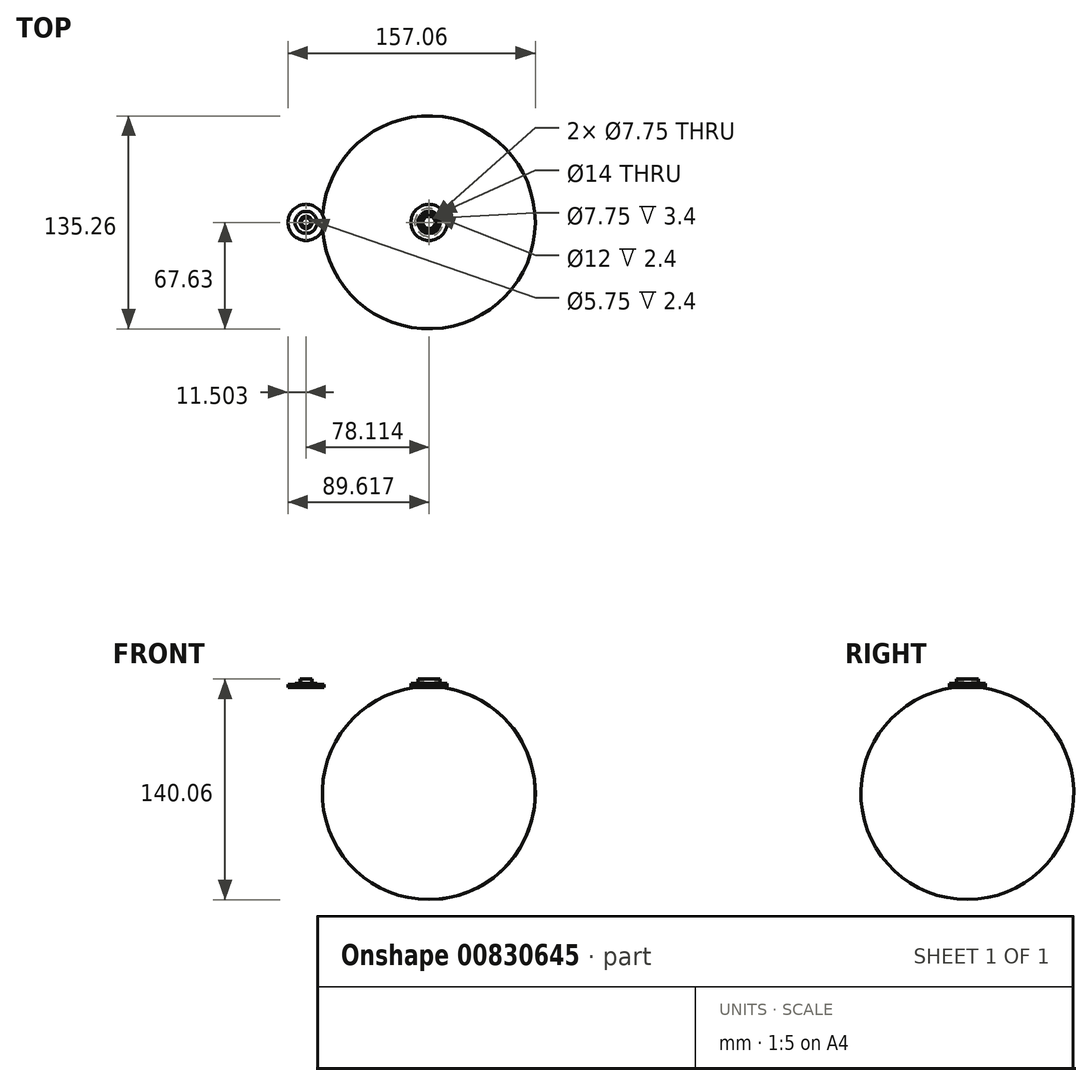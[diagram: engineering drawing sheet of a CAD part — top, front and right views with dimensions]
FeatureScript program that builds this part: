
annotation { "Feature Type Name" : "Feature", "Feature Type Description" : "" }
export const myFeature = defineFeature(function(context is Context, id is Id, definition is map)
    precondition{}
    {
        {
            var Q0;
            Q0=qCreatedBy(makeId("Top.planeOp"),FACE);
            var sketch = newSketch(context, id + "F0", { "sketchPlane" : qUnion([Q0])});
            skCircle(sketch, "E0", {"center": v(-39.06, 0) * mm, "radius": 3.88 * mm});
            skCircle(sketch, "E1", {"center": v(-39.06, 0) * mm, "radius": 7 * mm});
            skCircle(sketch, "E2", {"center": v(-39.06, 0) * mm, "radius": 11.5 * mm});
            skCircle(sketch, "E3.MirrorC", {"center": v(39.06, 0) * mm, "radius": 11.5 * mm});
            skCircle(sketch, "E4.MirrorC", {"center": v(39.06, 0) * mm, "radius": 7 * mm});
            skCircle(sketch, "E5.MirrorC", {"center": v(39.06, 0) * mm, "radius": 3.88 * mm});
            skSolve(sketch);
        }
        {
            var Q0;
            Q0=makeQuery(id+"F0.imprint","IMPRINT",FACE,{"disambiguationData":[TD([[makeQuery(id+"F0.imprint","IMPRINT",EDGE,{"derivedFrom":sQuery(id+"F0.wireOp",EDGE,"E0")}),1.0]])]});
            var Q1;
            Q1=makeQuery(id+"F0.imprint","IMPRINT",FACE,{"disambiguationData":[TD([[makeQuery(id+"F0.imprint","IMPRINT",EDGE,{"derivedFrom":sQuery(id+"F0.wireOp",EDGE,"E5.MirrorC")}),-1.0]])]});
            extrude(context, id + "F1", {"entities" : qUnion([Q0, Q1]), "depth" : 3.4 * mm, "offsetDistance" : 25 * mm});
        }
        {
            var Q0;
            Q0=makeQuery(id+"F0.imprint","IMPRINT",FACE,{"disambiguationData":[TD([[makeQuery(id+"F0.imprint","IMPRINT",EDGE,{"derivedFrom":sQuery(id+"F0.wireOp",EDGE,"E0")}),-1.0]])]});
            var Q1;
            Q1=makeQuery(id+"F0.imprint","IMPRINT",FACE,{"disambiguationData":[TD([[makeQuery(id+"F0.imprint","IMPRINT",EDGE,{"derivedFrom":sQuery(id+"F0.wireOp",EDGE,"E4.MirrorC")}),-1.0]])]});
            extrude(context, id + "F2", {"entities" : qUnion([Q0, Q1]), "depth" : 0.6 * mm, "offsetDistance" : 25 * mm});
        }
        {
            var Q0;
            Q0=makeQuery(id+"F0.imprint","IMPRINT",FACE,{"disambiguationData":[TD([[makeQuery(id+"F0.imprint","IMPRINT",EDGE,{"derivedFrom":sQuery(id+"F0.wireOp",EDGE,"E1")}),-1.0]])]});
            var Q1;
            Q1=makeQuery(id+"F0.imprint","IMPRINT",FACE,{"disambiguationData":[TD([[makeQuery(id+"F0.imprint","IMPRINT",EDGE,{"derivedFrom":sQuery(id+"F0.wireOp",EDGE,"E3.MirrorC")}),-1.0]])]});
            var Q2;
            Q2=makeQuery(id+"F0.imprint","IMPRINT",FACE,{"disambiguationData":[TD([[makeQuery(id+"F0.imprint","IMPRINT",EDGE,{"derivedFrom":sQuery(id+"F0.wireOp",EDGE,"E0")}),-1.0]])]});
            var Q3;
            Q3=makeQuery(id+"F0.imprint","IMPRINT",FACE,{"disambiguationData":[TD([[makeQuery(id+"F0.imprint","IMPRINT",EDGE,{"derivedFrom":sQuery(id+"F0.wireOp",EDGE,"E0")}),1.0]])]});
            var Q4;
            Q4=makeQuery(id+"F0.imprint","IMPRINT",FACE,{"disambiguationData":[TD([[makeQuery(id+"F0.imprint","IMPRINT",EDGE,{"derivedFrom":sQuery(id+"F0.wireOp",EDGE,"E4.MirrorC")}),-1.0]])]});
            var Q5;
            Q5=makeQuery(id+"F0.imprint","IMPRINT",FACE,{"disambiguationData":[TD([[makeQuery(id+"F0.imprint","IMPRINT",EDGE,{"derivedFrom":sQuery(id+"F0.wireOp",EDGE,"E5.MirrorC")}),-1.0]])]});
            extrude(context, id + "F3", {"entities" : qUnion([Q0, Q1, Q2, Q3, Q4, Q5]), "oppositeDirection" : true, "depth" : 2 * mm, "offsetDistance" : 25 * mm});
        }
        {
            var Q0;
            Q0=makeQuery(id+"F1.opExtrude","CAP_FACE",FACE,{"disambiguationData":[OSD([sQuery(id+"F0.wireOp",EDGE,"E0")])],"isStart":false});
            var Q1;
            Q1=makeQuery(id+"F1.opExtrude","CAP_FACE",FACE,{"disambiguationData":[OSD([sQuery(id+"F0.wireOp",EDGE,"E5.MirrorC")])],"isStart":false});
            shell(context, id + "F4", {"entities" : qUnion([Q0, Q1]), "thickness" : 1 * mm});
        }
        {
            var Q0;
            Q0=qCreatedBy(makeId("Front.planeOp"),FACE);
            var sketch = newSketch(context, id + "F5", { "sketchPlane" : qUnion([Q0])});
            skLineSegment(sketch, "E6", {"start": v(38.88, 0) * mm, "end": v(38.88, 54.86) * mm});
            skLineSegment(sketch, "E7", {"start": v(38.88, -1.4) * mm, "end": v(38.88, 0) * mm});
            skArc(sketch, "E8", {"start": v(38.88, -136.66) * mm, "mid": v(106.5, -69.03) * mm, "end": v(38.88, -1.4) * mm});
            skPoint(sketch, "E9.orphan", {"position": v(38.88, -55.04) * mm});
            skLineSegment(sketch, "E10", {"start": v(38.88, -1.4) * mm, "end": v(38.88, -69.03) * mm});
            skLineSegment(sketch, "E11", {"start": v(38.88, -69.03) * mm, "end": v(38.88, -136.66) * mm});
            skSolve(sketch);
        }
        {
            var Q0;
            Q0=makeQuery(id+"F5.imprint","IMPRINT",FACE,{"disambiguationData":[TD([[makeQuery(id+"F5.imprint","IMPRINT",EDGE,{"derivedFrom":sQuery(id+"F5.wireOp",EDGE,"E8")}),1.0]])]});
            var Q1;
            Q1=sQuery(id+"F5.wireOp",EDGE,"E11");
            revolve(context, id + "F6", {"operationType" : NewBodyOperationType.ADD, "surfaceOperationType" : NewSurfaceOperationType.NEW, "entities" : qUnion([Q0]), "axis" : qUnion([Q1]), "revolveType" : RevolveType.FULL});
        }
    });
